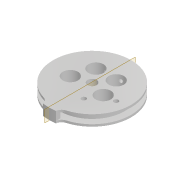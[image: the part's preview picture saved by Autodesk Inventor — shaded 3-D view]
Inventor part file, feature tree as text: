
AUTODESK INVENTOR PART (.ipt)
format: ipt  version: 2022 (Build 260153000, 153)  size: 299,520 bytes
history: native  units: mm
features: extrude x8, sketch x7, plane x3, fillet x2, pattern_circular x1, mirror x1, projected_geometry x1
ambient origin geometry x8: Origin, YZ Plane, XZ Plane, XY Plane, X Axis, Y Axis, Z Axis, Center Point
bodies: Solid1 (feature_tree)
feature tree (23):
  extrude  "Extrusion1"  Depth=30.0mm
  extrude  "Extrusion2"  Depth=3.0mm TaperAngle=0.0deg
  pattern_circular  "Circular Pattern1"  Count=5 Angle=360.0deg
  plane  "Work Plane1"
  plane  "Work Plane2"
  extrude  "Extrusion3"  [1 undecoded]
  extrude  "Extrusion4"  Depth=3.0mm
  fillet  "Fillet1"  Radius=1.7mm
  plane  "Work Plane3"
  extrude  "Extrusion5"  Depth=10.0mm TaperAngle=0.0deg
  mirror  "Mirror1"
  sketch  "Sketch6"  dims[d13=9.599311mm d14=-9.599311mm]
  extrude  "Extrusion6"  Depth=3.0mm
  extrude  "Extrusion7"  Depth=3.0mm
  extrude  "Extrusion8"  Depth=3.0mm
  fillet  "Fillet2"  Radius=10.0mm
  sketch  "Sketch1"  dims[d0=4.2mm d2=30.0mm]
  sketch  "Sketch2"  dims[d3=4.0mm d4=3.0mm d5=0.0mm]
  sketch  "Sketch3"  dims[d6=7.0mm]
  sketch  "Sketch4"  dims[d7=8.0mm]
  sketch  "Sketch5"  dims[d8=10.0mm d9=0.0mm d10=50.0mm d11=360.0deg]
  projected_geometry  "Projected Loop1"
  sketch  "Sketch7"  dims[d15=1.5mm d16=1.5mm d17=1.7mm d18=10.0mm d19=0.0mm d20=1.5mm d21=1.5mm d22=1.7mm d23=10.0mm d24=0.0mm d25=1.0mm d26=36.0mm d27=1.0mm d28=0.0mm d29=2.1mm d30=13.0mm d31=1.9mm d32=2.1mm d33=8.4mm d35=5.0mm d36=0.0mm d37=100.0mm d38=0.0mm d39=4.5mm d40=3.0mm d41=3.0mm d42=2.0mm d43=5.0mm d44=0.0mm d45=3.0mm]
note: 1 required parameter value undecoded (feature->parameter linkage not recoverable at this tier; creation-order binding heuristic only, values carry confidence <= 0.55)
